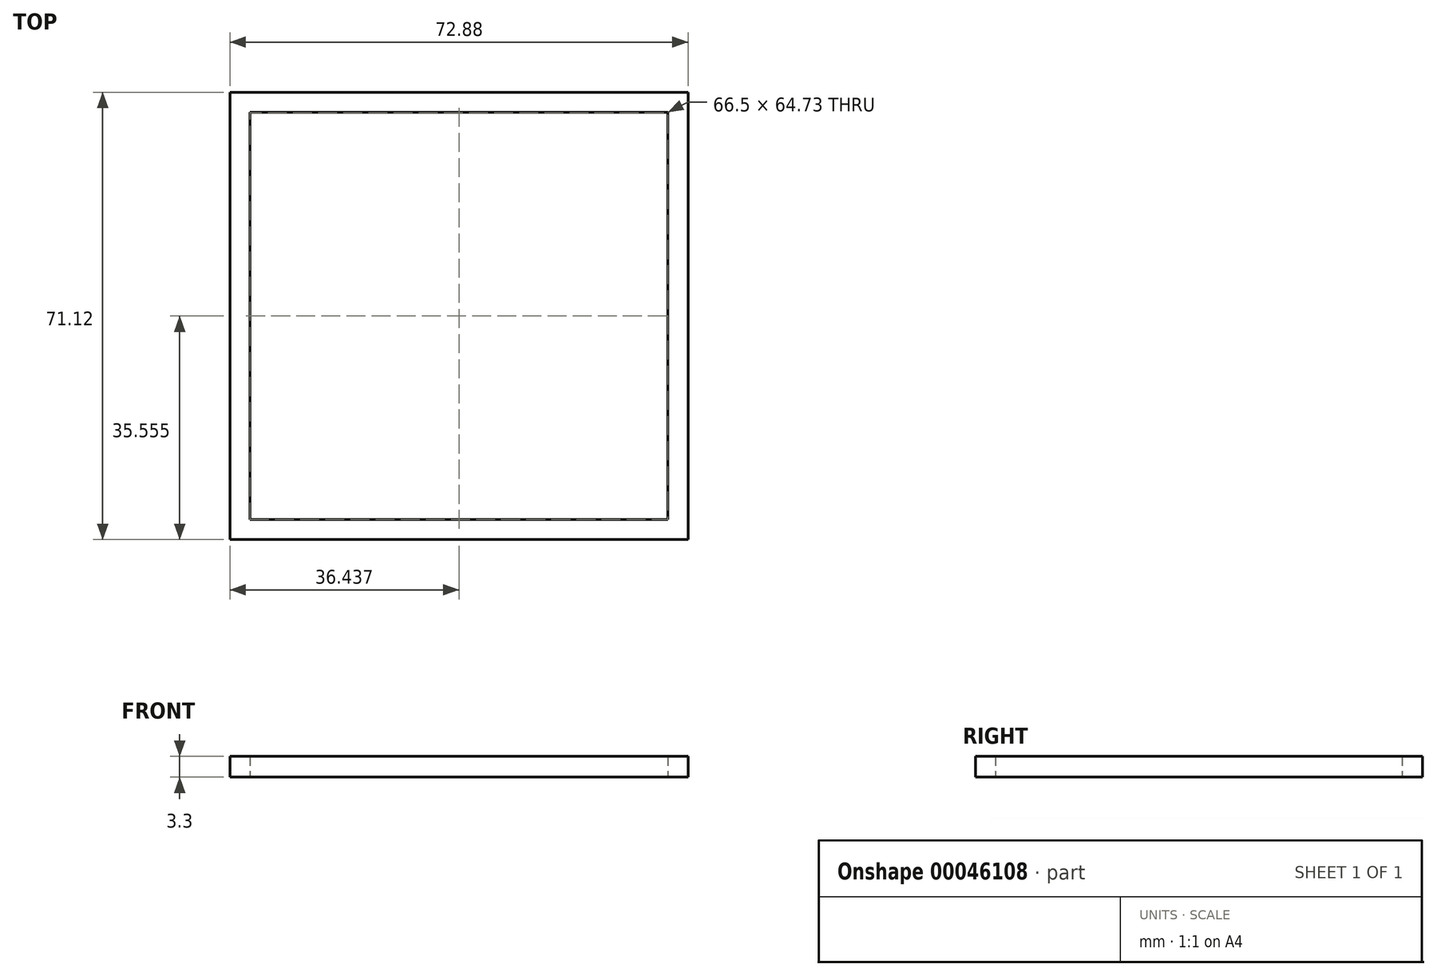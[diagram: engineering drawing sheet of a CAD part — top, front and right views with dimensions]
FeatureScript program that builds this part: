
annotation { "Feature Type Name" : "Feature", "Feature Type Description" : "" }
export const myFeature = defineFeature(function(context is Context, id is Id, definition is map)
    precondition{}
    {
        {
            var Q0;
            Q0=qCreatedBy(makeId("Top.planeOp"),FACE);
            var sketch = newSketch(context, id + "F0", { "sketchPlane" : qUnion([Q0])});
            skLineSegment(sketch, "E0", {"start": v(-26.7, 18.81) * mm, "end": v(46.18, 18.81) * mm});
            skLineSegment(sketch, "E1", {"start": v(46.18, 18.81) * mm, "end": v(46.18, -52.3) * mm});
            skLineSegment(sketch, "E2", {"start": v(46.18, -52.3) * mm, "end": v(-26.7, -52.3) * mm});
            skLineSegment(sketch, "E3", {"start": v(-26.7, -52.3) * mm, "end": v(-26.7, 18.81) * mm});
            skLineSegment(sketch, "E4", {"start": v(-23.51, 15.6) * mm, "end": v(-23.51, -49.12) * mm});
            skLineSegment(sketch, "E5", {"start": v(-23.51, -49.12) * mm, "end": v(42.99, -49.12) * mm});
            skLineSegment(sketch, "E6", {"start": v(42.99, -49.12) * mm, "end": v(42.99, 15.6) * mm});
            skLineSegment(sketch, "E7", {"start": v(42.99, 15.6) * mm, "end": v(-23.51, 15.6) * mm});
            skSolve(sketch);
        }
        {
            var Q0;
            Q0 = qSketchRegion(id + "F0", true);
            extrude(context, id + "F1", {"entities" : qUnion([Q0]), "depth" : 3.3 * mm});
        }
    });
